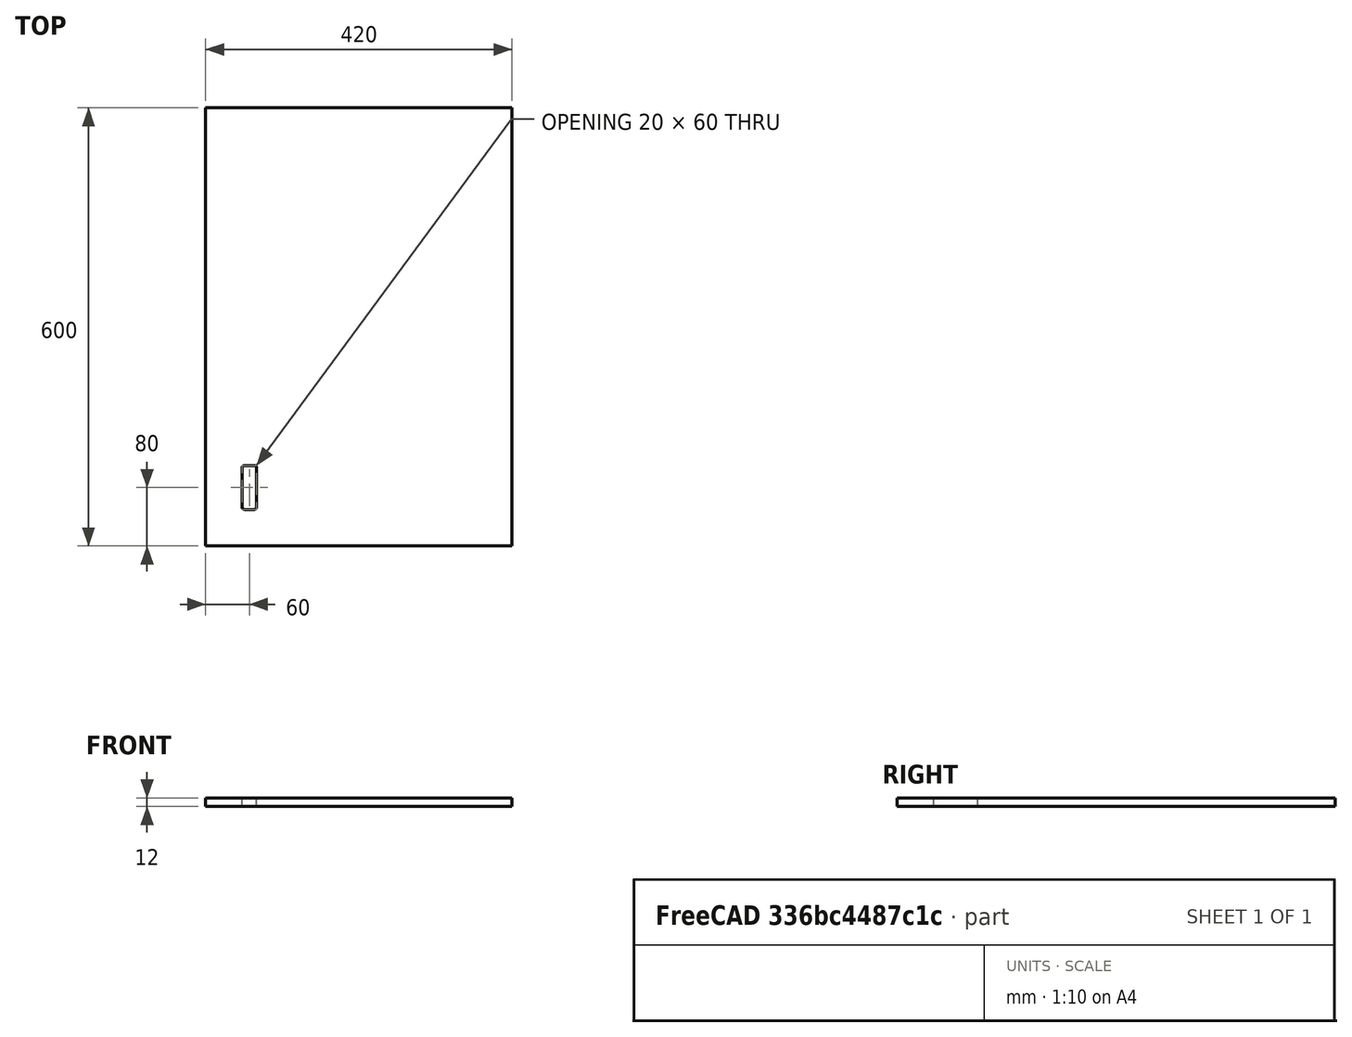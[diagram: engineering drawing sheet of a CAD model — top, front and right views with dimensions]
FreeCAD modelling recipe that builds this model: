
FCSTD DOCUMENT  (FreeCAD 0.18R16131 (Git))
Label: Back_plate
License: All rights reserved
LicenseURL: http://en.wikipedia.org/wiki/All_rights_reserved
objects: Sketcher::SketchObject×1, PartDesign::Pad×1, PartDesign::Body×1
note: 4 computed .brp shape members not serialized (recipe doc carries the construction recipe); baked Part::Feature solids carry a one-line shape summary decoded from their .brp

FEATURE [Sketcher::SketchObject] Sketch
  MapMode = 5
  Support = -> [XY_Plane]
  sketch-geometry (12):
    g0: LineSegment StartX=0 StartY=0 StartZ=0 EndX=420 EndY=0 EndZ=0
    g1: LineSegment StartX=420 StartY=0 StartZ=0 EndX=420 EndY=600 EndZ=0
    g2: LineSegment StartX=420 StartY=600 StartZ=0 EndX=0 EndY=600 EndZ=0
    g3: LineSegment StartX=0 StartY=600 StartZ=0 EndX=0 EndY=0 EndZ=0
    g4: LineSegment StartX=50 StartY=107 StartZ=0 EndX=50 EndY=53 EndZ=0
    g5: LineSegment StartX=70 StartY=107 StartZ=0 EndX=70 EndY=53 EndZ=0
    g6: ArcOfCircle CenterX=53 CenterY=107 CenterZ=0 NormalX=0 NormalY=0 NormalZ=1 AngleXU=0 Radius=3 StartAngle=1.5708 EndAngle=3.14159
    g7: ArcOfCircle CenterX=67 CenterY=107 CenterZ=0 NormalX=0 NormalY=0 NormalZ=1 AngleXU=0 Radius=3 StartAngle=0 EndAngle=1.5708
    g8: LineSegment StartX=53 StartY=110 StartZ=0 EndX=67 EndY=110 EndZ=0
    g9: ArcOfCircle CenterX=53 CenterY=53 CenterZ=0 NormalX=0 NormalY=0 NormalZ=1 AngleXU=0 Radius=3 StartAngle=3.14159 EndAngle=4.71239
    g10: ArcOfCircle CenterX=67 CenterY=53 CenterZ=0 NormalX=0 NormalY=0 NormalZ=1 AngleXU=0 Radius=3 StartAngle=4.71239 EndAngle=6.28319
    g11: LineSegment StartX=53 StartY=50 StartZ=0 EndX=67 EndY=50 EndZ=0
  constraints (39):
    c: Coincident(g0,g1)
    c: Coincident(g1,g2)
    c: Coincident(g2,g3)
    c: Coincident(g3,g0)
    c: Horizontal(g0)
    c: Horizontal(g2)
    c: Vertical(g1)
    c: Vertical(g3)
    c: Coincident(g0,g-1)
    c: DistanceX(g2,g2) = 420
    c: DistanceY(g3,g3) = 600
    c: Vertical(g4)
    c: Vertical(g5)
    c: Coincident(g4,g6)
    c: Horizontal(g4,g6)
    c: Vertical(g6,g6)
    c: Equal(g6,g7)
    c: Coincident(g7,g5)
    c: Horizontal(g6,g7)
    c: Coincident(g8,g6)
    c: Coincident(g8,g7)
    c: Horizontal(g8)
    c: Coincident(g4,g9)
    c: Horizontal(g4,g9)
    c: Vertical(g9,g9)
    c: Equal(g7,g9)
    c: Coincident(g5,g10)
    c: Coincident(g11,g9)
    c: Coincident(g11,g10)
    c: Horizontal(g11)
    c: Horizontal(g10,g9)
    c: Horizontal(g10,g5)
    c: Vertical(g10,g10)
    c: Horizontal(g7,g5)
    c: DistanceX(g4,g5) = 20
    c: Radius(g6) = 3
    c: DistanceY(g9,g6) = 60
    c: DistanceY(g0,g9) = 50
    c: DistanceX(g0,g4) = 50
FEATURE [PartDesign::Pad] Pad
  Length = 12
  Length2 = 100
  Profile = -> Sketch
  Type = 0
FEATURE [PartDesign::Body] Body
  Group = -> [Sketch,Pad]
  Origin = -> Origin
  Tip = -> Pad
